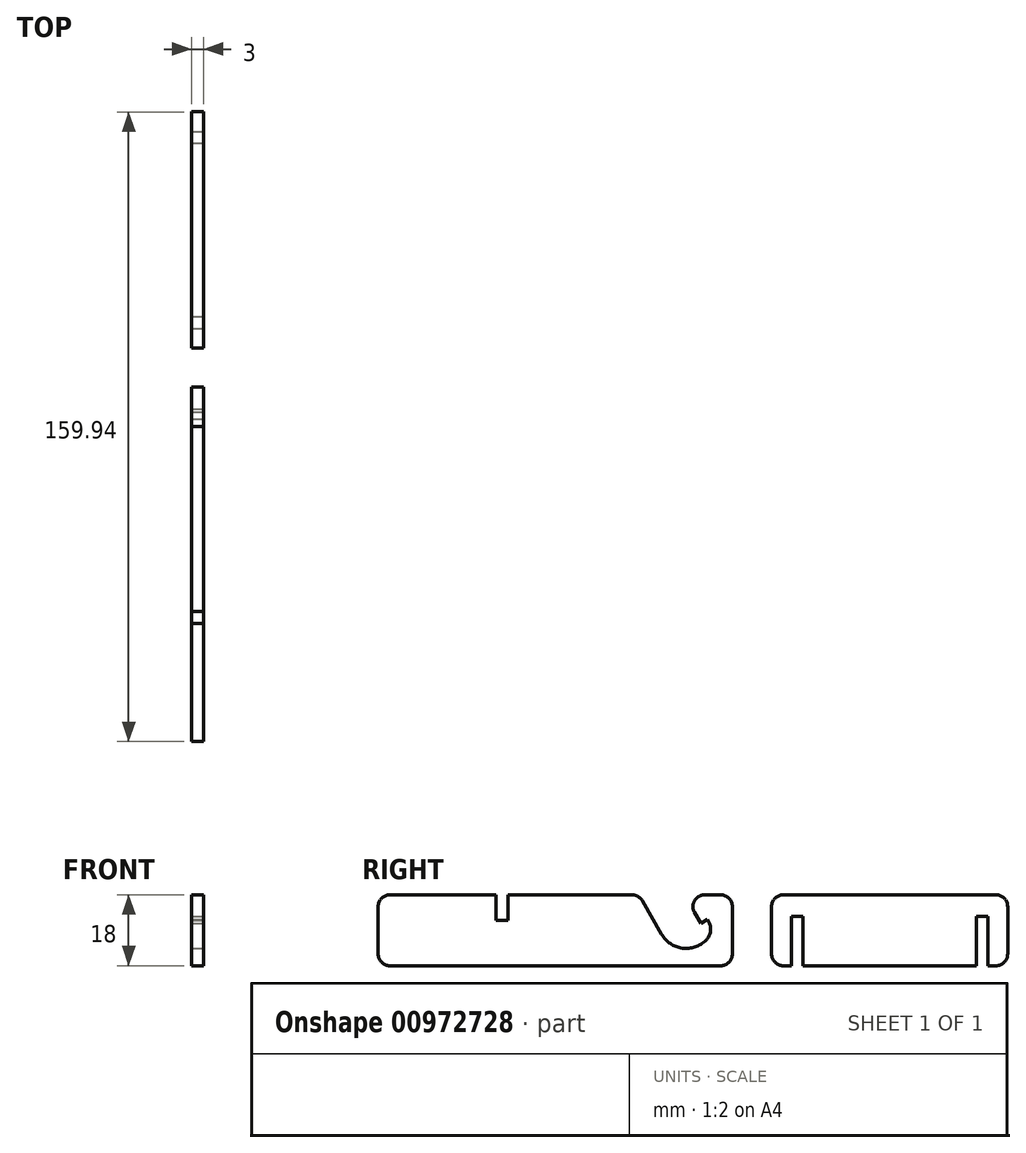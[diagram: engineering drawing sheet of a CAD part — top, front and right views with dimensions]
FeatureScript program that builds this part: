
annotation { "Feature Type Name" : "Feature", "Feature Type Description" : "" }
export const myFeature = defineFeature(function(context is Context, id is Id, definition is map)
    precondition{}
    {
        {
            var Q0;
            Q0=qCreatedBy(makeId("Right.planeOp"),FACE);
            var sketch = newSketch(context, id + "F0", { "sketchPlane" : qUnion([Q0])});
            skLineSegment(sketch, "E0.bottom", {"start": v(-90, 0) * mm, "end": v(0, 0) * mm});
            skLineSegment(sketch, "E0.top", {"start": v(-90, 18) * mm, "end": v(0, 18) * mm});
            skLineSegment(sketch, "E0.left", {"start": v(-90, 0) * mm, "end": v(-90, 18) * mm});
            skLineSegment(sketch, "E0.right", {"start": v(0, 0) * mm, "end": v(0, 18) * mm});
            skLineSegment(sketch, "E1.bottom", {"start": v(9.94, 0) * mm, "end": v(69.94, 0) * mm});
            skLineSegment(sketch, "E1.top", {"start": v(9.94, 18) * mm, "end": v(69.94, 18) * mm});
            skLineSegment(sketch, "E1.left", {"start": v(9.94, 0) * mm, "end": v(9.94, 18) * mm});
            skLineSegment(sketch, "E1.right", {"start": v(69.94, 0) * mm, "end": v(69.94, 18) * mm});
            skSolve(sketch);
        }
        {
            var Q0;
            Q0 = qSketchRegion(id + "F0", true);
            extrude(context, id + "F1", {"entities" : qUnion([Q0]), "depth" : 3 * mm, "offsetDistance" : 25 * mm});
        }
        {
            var Q0;
            Q0=makeQuery(id+"F1.opExtrude","CAP_FACE",FACE,{"disambiguationData":[OSD([sQuery(id+"F0.wireOp",EDGE,"E0.bottom"),sQuery(id+"F0.wireOp",EDGE,"E0.top"),sQuery(id+"F0.wireOp",EDGE,"E0.left"),sQuery(id+"F0.wireOp",EDGE,"E0.right")])],"isStart":false});
            var sketch = newSketch(context, id + "F2", { "sketchPlane" : qUnion([Q0])});
            skLineSegment(sketch, "E2", {"start": v(-30.5, 29.65) * mm, "end": v(-18, 8) * mm});
            skLineSegment(sketch, "E3", {"start": v(-6.3, 11.75) * mm, "end": v(-8.04, 10.75) * mm});
            skLineSegment(sketch, "E4", {"start": v(-8.04, 10.75) * mm, "end": v(-18.95, 29.65) * mm});
            skLineSegment(sketch, "E5", {"start": v(-18.95, 29.65) * mm, "end": v(-30.5, 29.65) * mm});
            skLineSegment(sketch, "E6", {"start": v(-6.3, 11.75) * mm, "end": v(-6.06, 11.32) * mm});
            skArc(sketch, "E7", {"start": v(-6.06, 11.32) * mm, "mid": v(-5.56, 8.78) * mm, "end": v(-6.72, 6.46) * mm});
            skArc(sketch, "E8", {"start": v(-6.72, 6.46) * mm, "mid": v(-12.74, 4.47) * mm, "end": v(-18, 8) * mm});
            skSolve(sketch);
        }
        {
            var Q0;
            Q0 = qSketchRegion(id + "F2", true);
            extrude(context, id + "F3", {"entities" : qUnion([Q0]), "operationType" : NewBodyOperationType.REMOVE, "endBound" : BoundingType.THROUGH_ALL, "oppositeDirection" : true, "depth" : 25 * mm, "offsetDistance" : 25 * mm});
        }
        {
            var Q0;
            Q0=makeQuery(id+"F3.boolean.opBoolean","INTERSECT",EDGE,{"derivedFrom":[makeQuery(id+"F1.opExtrude","SWEPT_FACE",FACE,{"disambiguationData":[OSD([sQuery(id+"F0.wireOp",EDGE,"E0.top")])]}),makeQuery(id+"F3.opExtrude","SWEPT_FACE",FACE,{"disambiguationData":[OSD([sQuery(id+"F2.wireOp",EDGE,"E4")])]})]});
            var Q1;
            Q1=makeQuery(id+"F1.opExtrude","SWEPT_EDGE",EDGE,{"disambiguationData":[OSD([sQuery(id+"F0.wireOp",EDGE,"E0.top"),sQuery(id+"F0.wireOp",EDGE,"E0.right")])]});
            var Q2;
            Q2=makeQuery(id+"F3.boolean.opBoolean","INTERSECT",EDGE,{"derivedFrom":[makeQuery(id+"F1.opExtrude","SWEPT_FACE",FACE,{"disambiguationData":[OSD([sQuery(id+"F0.wireOp",EDGE,"E0.top")])]}),makeQuery(id+"F3.opExtrude","SWEPT_FACE",FACE,{"disambiguationData":[OSD([sQuery(id+"F2.wireOp",EDGE,"E2")])]})]});
            var Q3;
            Q3=makeQuery(id+"F1.opExtrude","SWEPT_EDGE",EDGE,{"disambiguationData":[OSD([sQuery(id+"F0.wireOp",EDGE,"E0.bottom"),sQuery(id+"F0.wireOp",EDGE,"E0.right")])]});
            var Q4;
            Q4=makeQuery(id+"F1.opExtrude","SWEPT_EDGE",EDGE,{"disambiguationData":[OSD([sQuery(id+"F0.wireOp",EDGE,"E0.top"),sQuery(id+"F0.wireOp",EDGE,"E0.left")])]});
            var Q5;
            Q5=makeQuery(id+"F1.opExtrude","SWEPT_EDGE",EDGE,{"disambiguationData":[OSD([sQuery(id+"F0.wireOp",EDGE,"E0.bottom"),sQuery(id+"F0.wireOp",EDGE,"E0.left")])]});
            var Q6;
            Q6=makeQuery(id+"F1.opExtrude","SWEPT_EDGE",EDGE,{"disambiguationData":[OSD([sQuery(id+"F0.wireOp",EDGE,"E1.top"),sQuery(id+"F0.wireOp",EDGE,"E1.right")])]});
            var Q7;
            Q7=makeQuery(id+"F1.opExtrude","SWEPT_EDGE",EDGE,{"disambiguationData":[OSD([sQuery(id+"F0.wireOp",EDGE,"E1.bottom"),sQuery(id+"F0.wireOp",EDGE,"E1.right")])]});
            var Q8;
            Q8=makeQuery(id+"F1.opExtrude","SWEPT_EDGE",EDGE,{"disambiguationData":[OSD([sQuery(id+"F0.wireOp",EDGE,"E1.bottom"),sQuery(id+"F0.wireOp",EDGE,"E1.left")])]});
            var Q9;
            Q9=makeQuery(id+"F1.opExtrude","SWEPT_EDGE",EDGE,{"disambiguationData":[OSD([sQuery(id+"F0.wireOp",EDGE,"E1.top"),sQuery(id+"F0.wireOp",EDGE,"E1.left")])]});
            fillet(context, id + "F4", {"entities" : qUnion([Q0, Q1, Q2, Q3, Q4, Q5, Q6, Q7, Q8, Q9]), "radius" : 3 * mm, "tangentPropagation" : true, "allowEdgeOverflow" : false});
        }
        {
            var Q0;
            Q0=makeQuery(id+"F1.opExtrude","CAP_FACE",FACE,{"disambiguationData":[OSD([sQuery(id+"F0.wireOp",EDGE,"E0.bottom"),sQuery(id+"F0.wireOp",EDGE,"E0.top"),sQuery(id+"F0.wireOp",EDGE,"E0.left"),sQuery(id+"F0.wireOp",EDGE,"E0.right")])],"isStart":false});
            var sketch = newSketch(context, id + "F5", { "sketchPlane" : qUnion([Q0])});
            skLineSegment(sketch, "E9.bottom", {"start": v(-60, 18) * mm, "end": v(-57, 18) * mm});
            skLineSegment(sketch, "E9.top", {"start": v(-60, 11.5) * mm, "end": v(-57, 11.5) * mm});
            skLineSegment(sketch, "E9.left", {"start": v(-60, 18) * mm, "end": v(-60, 11.5) * mm});
            skLineSegment(sketch, "E9.right", {"start": v(-57, 18) * mm, "end": v(-57, 11.5) * mm});
            skLineSegment(sketch, "E10.bottom", {"start": v(14.94, 0) * mm, "end": v(17.94, 0) * mm});
            skLineSegment(sketch, "E10.top", {"start": v(14.94, 12.5) * mm, "end": v(17.94, 12.5) * mm});
            skLineSegment(sketch, "E10.left", {"start": v(14.94, 0) * mm, "end": v(14.94, 12.5) * mm});
            skLineSegment(sketch, "E10.right", {"start": v(17.94, 0) * mm, "end": v(17.94, 12.5) * mm});
            skLineSegment(sketch, "E11.bottom", {"start": v(61.94, 0) * mm, "end": v(64.94, 0) * mm});
            skLineSegment(sketch, "E11.top", {"start": v(61.94, 12.5) * mm, "end": v(64.94, 12.5) * mm});
            skLineSegment(sketch, "E11.left", {"start": v(61.94, 0) * mm, "end": v(61.94, 12.5) * mm});
            skLineSegment(sketch, "E11.right", {"start": v(64.94, 0) * mm, "end": v(64.94, 12.5) * mm});
            skSolve(sketch);
        }
        {
            var Q0;
            Q0 = qSketchRegion(id + "F5", true);
            extrude(context, id + "F6", {"entities" : qUnion([Q0]), "operationType" : NewBodyOperationType.REMOVE, "endBound" : BoundingType.THROUGH_ALL, "oppositeDirection" : true, "depth" : 25 * mm, "offsetDistance" : 25 * mm});
        }
    });
